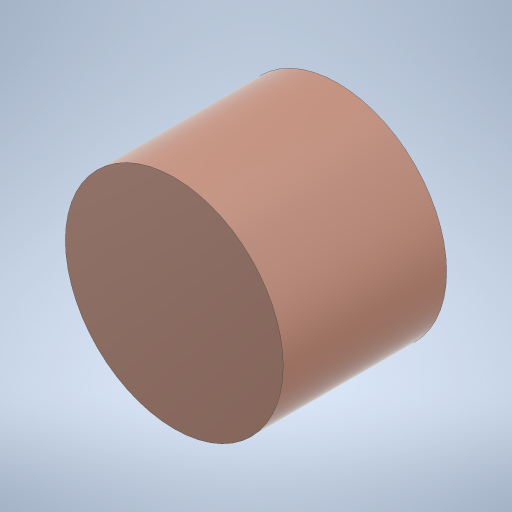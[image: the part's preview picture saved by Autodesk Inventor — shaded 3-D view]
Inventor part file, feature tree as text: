
AUTODESK INVENTOR PART (.ipt)
format: ipt  version: 2023 (Build 270158000, 158)  size: 237,568 bytes
history: native  units: in
note: dims shown in document units (in); Inventor stores cm internally (conversion verified against a paired STEP export)
features: sketch x2, extrude x1, hole x1, thread x1
ambient origin geometry x8: Origin, YZ Plane, XZ Plane, XY Plane, X Axis, Y Axis, Z Axis, Center Point
bodies: Solid1 (feature_tree)
feature tree (5):
  extrude  "Extrusion1"  Depth=0.5906in TaperAngle=0.0deg
  hole  "Hole1"  [1 undecoded]
  thread  "Thread1"  [1 undecoded]
  sketch  "Sketch1"  dims[d0=0.7874in d1=0.5906in d2=0.0in]
  sketch  "Sketch2"  dims[d3=0.1181in d4=0.75in d5=0.375in d6=0.25in d7=0.5635in d8=0.2362in d9=0.8108in d10=3.0in d11=0.0in d12=0.0625in d13=0.75in d14=0.375in]
note: 2 required parameter values undecoded (feature->parameter linkage not recoverable at this tier; creation-order binding heuristic only, values carry confidence <= 0.55)
